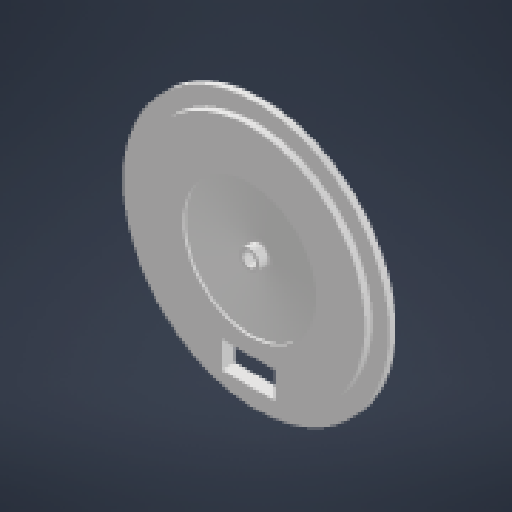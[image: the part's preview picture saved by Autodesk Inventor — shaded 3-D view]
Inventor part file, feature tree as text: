
AUTODESK INVENTOR PART (.ipt)
format: ipt  version: 2023 (Build 270158000, 158)  size: 227,840 bytes
history: native  units: mm
features: extrude x5, sketch x5, chamfer x1
ambient origin geometry x8: Origin, YZ Plane, XZ Plane, XY Plane, X Axis, Y Axis, Z Axis, Center Point
bodies: Solid1 (feature_tree)
feature tree (11):
  extrude  "Extrusion1"  Depth=5.0mm TaperAngle=0.0deg
  extrude  "Extrusion2"  Depth=5.0mm TaperAngle=0.0deg
  extrude  "Extrusion3"  Depth=10.0mm TaperAngle=0.0deg
  extrude  "Extrusion4"  Depth=100.0mm
  chamfer  "Chamfer1"  Distance=7.0mm
  extrude  "Extrusion10"  Depth=10.0mm
  sketch  "Sketch1"  dims[d0=200.0mm d1=5.0mm d2=0.0mm]
  sketch  "Sketch2"  dims[d3=174.0mm d4=5.0mm d5=0.0mm]
  sketch  "Sketch3"  dims[d6=10.0mm d7=10.0mm d8=0.0mm]
  sketch  "Sketch4"  dims[d9=15.0mm d10=100.0mm d11=7.0mm d12=0.0mm]
  sketch  "Sketch10"  dims[d13=5.0mm d14=40.0mm d15=45.0deg d52=17.873mm d53=20.7525mm d54=40.151mm d55=20.0mm d56=10.0mm d57=0.0mm]
